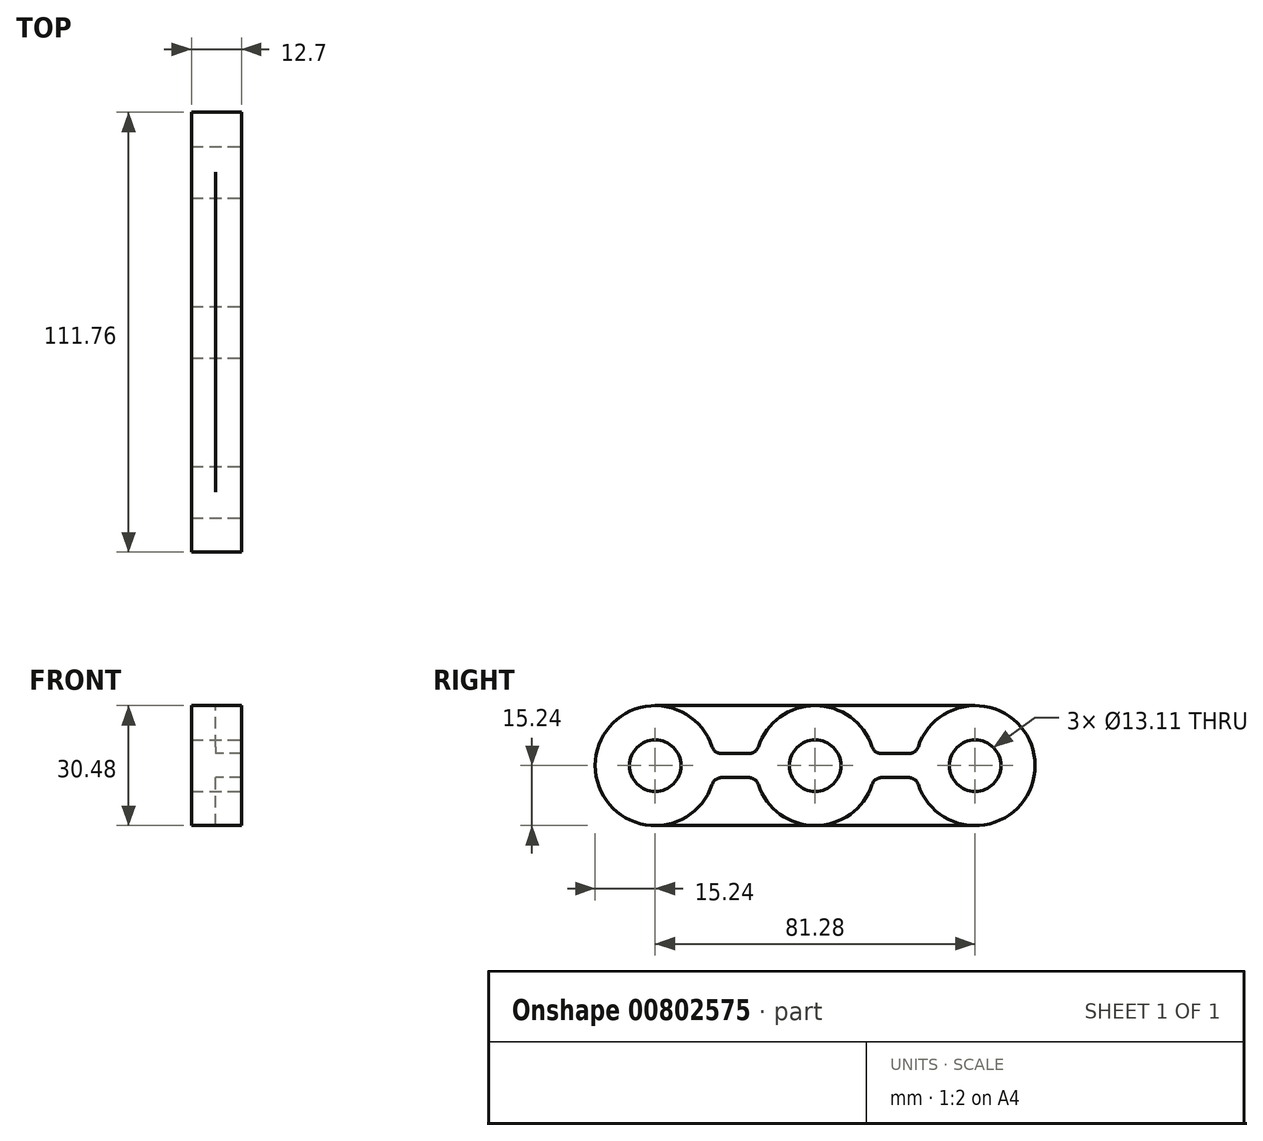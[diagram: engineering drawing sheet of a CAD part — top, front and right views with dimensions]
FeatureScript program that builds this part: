
annotation { "Feature Type Name" : "Feature", "Feature Type Description" : "" }
export const myFeature = defineFeature(function(context is Context, id is Id, definition is map)
    precondition{}
    {
        {
            var Q0;
            Q0=qCreatedBy(makeId("Right.planeOp"),FACE);
            var sketch = newSketch(context, id + "F0", { "sketchPlane" : qUnion([Q0])});
            skLineSegment(sketch, "E0", {"start": v(0, -22.48) * mm, "end": v(0, 22.07) * mm, "construction": true});
            skLineSegment(sketch, "E1", {"start": v(-54.4, 0) * mm, "end": v(65.01, 0) * mm, "construction": true});
            skLineSegment(sketch, "E2", {"start": v(-40.64, -6.7) * mm, "end": v(-40.64, 6.7) * mm, "construction": true});
            skLineSegment(sketch, "E3.MirrorCS", {"start": v(40.64, -6.7) * mm, "end": v(40.64, 6.7) * mm, "construction": true});
            skCircle(sketch, "E4", {"center": v(40.64, 0) * mm, "radius": 6.55 * mm});
            skCircle(sketch, "E5", {"center": v(0, 0) * mm, "radius": 6.55 * mm});
            skCircle(sketch, "E6", {"center": v(-40.64, 0) * mm, "radius": 6.55 * mm});
            skArc(sketch, "E7", {"start": v(-26.17, 4.79) * mm, "mid": v(-55.88, 0) * mm, "end": v(-26.17, -4.79) * mm});
            skArc(sketch, "E8", {"start": v(-14.47, -4.79) * mm, "mid": v(0, -15.24) * mm, "end": v(14.47, -4.79) * mm});
            skArc(sketch, "E9", {"start": v(26.17, -4.79) * mm, "mid": v(55.88, 0) * mm, "end": v(26.17, 4.79) * mm});
            skLineSegment(sketch, "E10", {"start": v(0, -15.24) * mm, "end": v(40.64, -15.24) * mm});
            skLineSegment(sketch, "E11", {"start": v(0, -15.24) * mm, "end": v(-40.64, -15.24) * mm});
            skLineSegment(sketch, "E12", {"start": v(-40.64, 15.24) * mm, "end": v(40.64, 15.24) * mm});
            skLineSegment(sketch, "E13", {"start": v(16.88, 3.05) * mm, "end": v(23.76, 3.05) * mm});
            skLineSegment(sketch, "E14", {"start": v(-16.88, 3.05) * mm, "end": v(-23.76, 3.05) * mm});
            skLineSegment(sketch, "E15.MirrorCS", {"start": v(-16.88, -3.05) * mm, "end": v(-23.76, -3.05) * mm});
            skLineSegment(sketch, "E16.MirrorCS", {"start": v(16.88, -3.05) * mm, "end": v(23.76, -3.05) * mm});
            skArc(sketch, "E17.trimOffspring", {"start": v(14.47, 4.79) * mm, "mid": v(0, 15.24) * mm, "end": v(-14.47, 4.79) * mm});
            skPoint(sketch, "E18.visualSharp", {"position": v(-14.93, -3.05) * mm});
            skArc(sketch, "E18.filletArc", {"start": v(-14.47, -4.79) * mm, "mid": v(-15.4, -3.53) * mm, "end": v(-16.88, -3.05) * mm});
            skPoint(sketch, "E19.visualSharp", {"position": v(-25.7, -3.05) * mm});
            skArc(sketch, "E19.filletArc", {"start": v(-23.76, -3.05) * mm, "mid": v(-25.25, -3.53) * mm, "end": v(-26.17, -4.79) * mm});
            skPoint(sketch, "E20.visualSharp", {"position": v(-25.7, 3.05) * mm});
            skArc(sketch, "E20.filletArc", {"start": v(-26.17, 4.79) * mm, "mid": v(-25.25, 3.53) * mm, "end": v(-23.76, 3.05) * mm});
            skPoint(sketch, "E21.visualSharp", {"position": v(-14.93, 3.05) * mm});
            skArc(sketch, "E21.filletArc", {"start": v(-16.88, 3.05) * mm, "mid": v(-15.4, 3.53) * mm, "end": v(-14.47, 4.79) * mm});
            skPoint(sketch, "E22.visualSharp", {"position": v(14.93, 3.05) * mm});
            skArc(sketch, "E22.filletArc", {"start": v(14.47, 4.79) * mm, "mid": v(15.4, 3.53) * mm, "end": v(16.88, 3.05) * mm});
            skPoint(sketch, "E23.visualSharp", {"position": v(14.93, -3.05) * mm});
            skArc(sketch, "E23.filletArc", {"start": v(16.88, -3.05) * mm, "mid": v(15.4, -3.53) * mm, "end": v(14.47, -4.79) * mm});
            skPoint(sketch, "E24.visualSharp", {"position": v(25.7, -3.05) * mm});
            skArc(sketch, "E24.filletArc", {"start": v(26.17, -4.79) * mm, "mid": v(25.25, -3.53) * mm, "end": v(23.76, -3.05) * mm});
            skPoint(sketch, "E25.visualSharp", {"position": v(25.7, 3.05) * mm});
            skArc(sketch, "E25.filletArc", {"start": v(23.76, 3.05) * mm, "mid": v(25.25, 3.53) * mm, "end": v(26.17, 4.79) * mm});
            skSolve(sketch);
        }
        {
            var Q0;
            Q0 = qSketchRegion(id + "F0", true);
            extrude(context, id + "F1", {"entities" : qUnion([Q0]), "oppositeDirection" : true, "depth" : 6.1 * mm, "offsetDistance" : 25.4 * mm});
        }
        {
            var Q0;
            Q0=makeQuery(id+"F0.imprint","IMPRINT",FACE,{"disambiguationData":[TD([[makeQuery(id+"F0.imprint","IMPRINT",EDGE,{"derivedFrom":sQuery(id+"F0.wireOp",EDGE,"E4")}),-1.0]])]});
            extrude(context, id + "F2", {"entities" : qUnion([Q0]), "operationType" : NewBodyOperationType.ADD, "depth" : 6.6 * mm, "offsetDistance" : 25.4 * mm});
        }
    });
